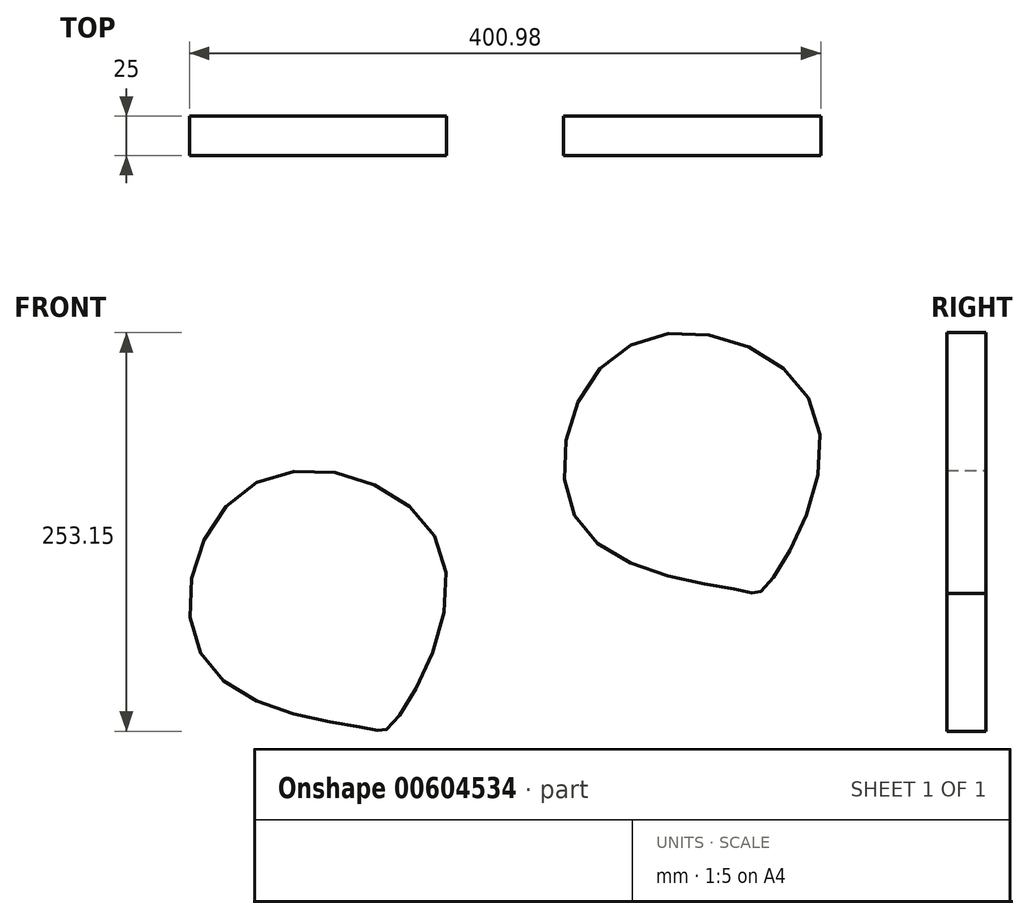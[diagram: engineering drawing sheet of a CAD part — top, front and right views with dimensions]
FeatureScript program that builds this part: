
annotation { "Feature Type Name" : "Feature", "Feature Type Description" : "" }
export const myFeature = defineFeature(function(context is Context, id is Id, definition is map)
    precondition{}
    {
        {
            var Q0;
            Q0=qCreatedBy(makeId("Front.planeOp"),FACE);
            var sketch = newSketch(context, id + "F0", { "sketchPlane" : qUnion([Q0])});
            skFitSpline(sketch, "E0", {"points": [v(-202.53, 84.47) * mm, v(-84.47, 38.76) * mm, v(-118.65, -71.35) * mm, v(-129.39, -72.15) * mm, v(-233.53, -31.2) * mm, v(-202.53, 84.47) * mm]});
            skFitSpline(sketch, "E1", {"points": [v(35.12, 172.03) * mm, v(153.18, 126.32) * mm, v(119, 16.21) * mm, v(108.26, 15.42) * mm, v(4.12, 56.36) * mm, v(35.12, 172.03) * mm]});
            skSolve(sketch);
        }
        {
            var Q0;
            Q0=qSketchRegion(id+"F0",true);
            extrude(context, id + "F1", {"entities" : qUnion([Q0]), "depth" : 25 * mm, "offsetDistance" : 25 * mm});
        }
    });
